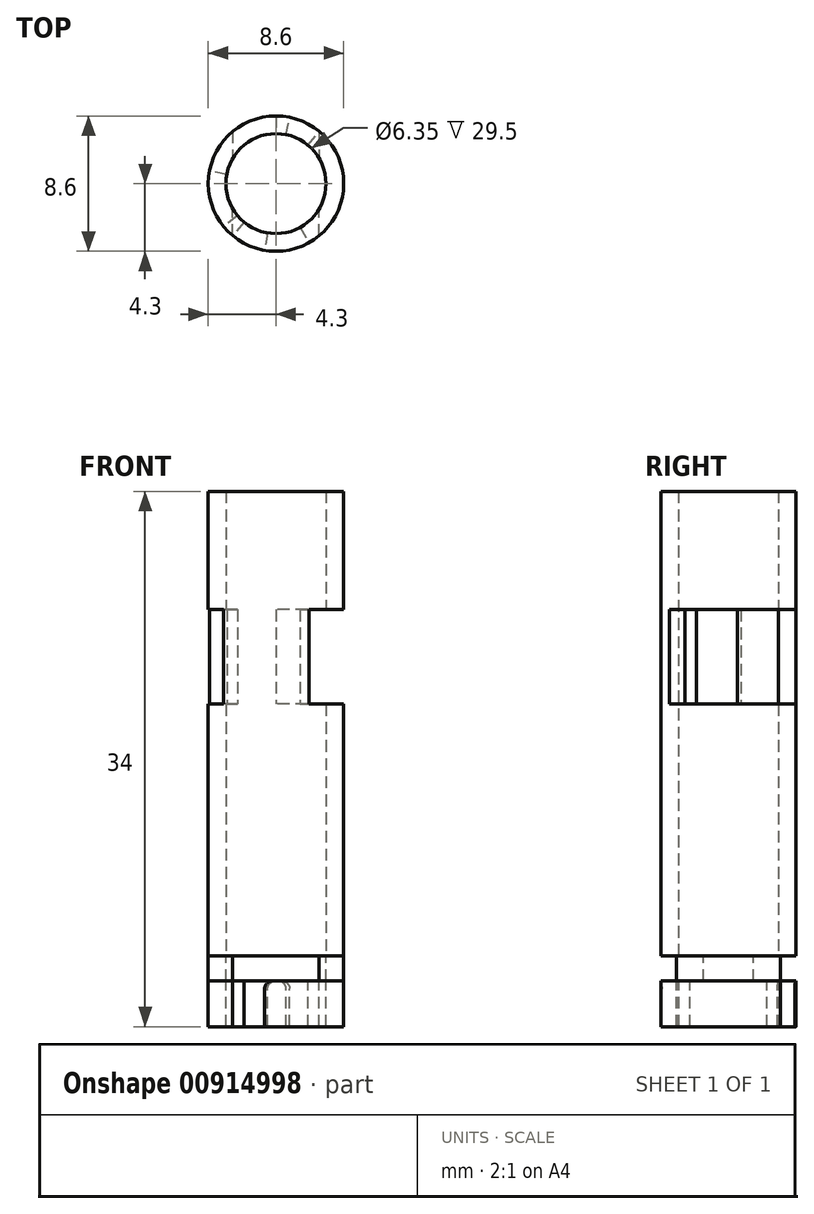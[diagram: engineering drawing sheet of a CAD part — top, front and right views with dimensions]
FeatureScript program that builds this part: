
annotation { "Feature Type Name" : "Feature", "Feature Type Description" : "" }
export const myFeature = defineFeature(function(context is Context, id is Id, definition is map)
    precondition{}
    {
        {
            var Q0;
            Q0=qCreatedBy(makeId("Top.planeOp"),FACE);
            var sketch = newSketch(context, id + "F0", { "sketchPlane" : qUnion([Q0])});
            skCircle(sketch, "E0", {"center": v(0, 0) * mm, "radius": 3.18 * mm});
            skCircle(sketch, "E1", {"center": v(0, 0) * mm, "radius": 4.3 * mm});
            skSolve(sketch);
        }
        {
            var Q0;
            Q0=makeQuery(id+"F0.imprint","IMPRINT",FACE,{"disambiguationData":[TD([[makeQuery(id+"F0.imprint","IMPRINT",EDGE,{"derivedFrom":sQuery(id+"F0.wireOp",EDGE,"E0")}),-1.0]])]});
            extrude(context, id + "F1", {"entities" : qUnion([Q0]), "depth" : 16 * mm, "offsetDistance" : 25.4 * mm});
        }
        {
            var Q0;
            Q0=makeQuery(id+"F1.opExtrude","CAP_FACE",FACE,{"disambiguationData":[OSD([sQuery(id+"F0.wireOp",EDGE,"E0"),sQuery(id+"F0.wireOp",EDGE,"E1")])],"isStart":false});
            var sketch = newSketch(context, id + "F2", { "sketchPlane" : qUnion([Q0])});
            skLineSegment(sketch, "E2", {"start": v(0, 4.3) * mm, "end": v(0, 3.17) * mm});
            skLineSegment(sketch, "E3", {"start": v(0, 0) * mm, "end": v(1.54, -2.78) * mm, "construction": true});
            skLineSegment(sketch, "E4", {"start": v(1.54, -2.78) * mm, "end": v(2.08, -3.76) * mm});
            skLineSegment(sketch, "E5", {"start": v(0, 0) * mm, "end": v(-2.45, -2.02) * mm});
            skLineSegment(sketch, "E6", {"start": v(0, 0) * mm, "end": v(-3.12, 0.58) * mm, "construction": true});
            skLineSegment(sketch, "E7", {"start": v(0, 3.17) * mm, "end": v(0, 0) * mm, "construction": true});
            skLineSegment(sketch, "E8", {"start": v(0, 0) * mm, "end": v(3.07, 0.8) * mm, "construction": true});
            skLineSegment(sketch, "E9", {"start": v(0, 0) * mm, "end": v(0.93, -3.04) * mm, "construction": true});
            skLineSegment(sketch, "E10", {"start": v(0.93, -3.04) * mm, "end": v(1.26, -4.11) * mm});
            skLineSegment(sketch, "E11", {"start": v(0, 0) * mm, "end": v(-1.54, 2.78) * mm, "construction": true});
            skLineSegment(sketch, "E12", {"start": v(0, 0) * mm, "end": v(-1.95, 2.5) * mm, "construction": true});
            skLineSegment(sketch, "E13", {"start": v(0, 0) * mm, "end": v(-1.09, 2.98) * mm, "construction": true});
            skLineSegment(sketch, "E14", {"start": v(-1.95, 2.5) * mm, "end": v(-2.65, 3.39) * mm});
            skLineSegment(sketch, "E15", {"start": v(-1.54, 2.78) * mm, "end": v(-2.08, 3.76) * mm});
            skLineSegment(sketch, "E16", {"start": v(-1.09, 2.98) * mm, "end": v(-1.47, 4.04) * mm});
            skLineSegment(sketch, "E17", {"start": v(0, 0) * mm, "end": v(-3.07, -0.8) * mm, "construction": true});
            skLineSegment(sketch, "E18", {"start": v(-3.12, 0.58) * mm, "end": v(-3.07, -0.8) * mm, "construction": true});
            skLineSegment(sketch, "E19", {"start": v(-3.07, -0.8) * mm, "end": v(-2.45, -2.02) * mm, "construction": true});
            skLineSegment(sketch, "E20", {"start": v(0, 3.17) * mm, "end": v(3.07, 0.8) * mm, "construction": true});
            skLineSegment(sketch, "E21", {"start": v(3.07, 0.8) * mm, "end": v(1.54, -2.78) * mm, "construction": true});
            skLineSegment(sketch, "E22", {"start": v(-3.12, 0.58) * mm, "end": v(-4.23, 0.78) * mm});
            skLineSegment(sketch, "E23", {"start": v(-2.45, -2.02) * mm, "end": v(-3.32, -2.74) * mm});
            skSolve(sketch);
        }
        {
            var Q0;
            {var subQ0=sQuery(id+"F2.wireOp",EDGE,"E2");Q0=makeQuery(id+"F2.imprint","IMPRINT",FACE,{"disambiguationData":[TD([[makeQuery(id+"F2.imprint","IMPRINT",EDGE,{"derivedFrom":subQ0}),-1.0]])]});}
            var Q1;
            {var subQ0=sQuery(id+"F2.wireOp",EDGE,"eu6biRq1-f5Uw-FhgU-ruvT-oJqhQKLmv7p4");Q1=makeQuery(id+"F2.imprint","IMPRINT",FACE,{"disambiguationData":[TD([[makeQuery(id+"F2.imprint","IMPRINT",EDGE,{"derivedFrom":subQ0}),1.0]])]});}
            var Q2;
            {var subQ0=sQuery(id+"F2.wireOp",EDGE,"E4");Q2=makeQuery(id+"F2.imprint","IMPRINT",FACE,{"disambiguationData":[TD([[makeQuery(id+"F2.imprint","IMPRINT",EDGE,{"derivedFrom":subQ0}),-1.0]])]});}
            var Q3;
            {var subQ0=sQuery(id+"F2.wireOp",EDGE,"WfiJlDDU-s9re-JO37-0JUV-52wj0VNvj8No");Q3=makeQuery(id+"F2.imprint","IMPRINT",FACE,{"disambiguationData":[TD([[makeQuery(id+"F2.imprint","IMPRINT",EDGE,{"derivedFrom":subQ0}),-1.0]])]});}
            var Q4;
            {var subQ0=sQuery(id+"F2.wireOp",EDGE,"E14");Q4=makeQuery(id+"F2.imprint","IMPRINT",FACE,{"disambiguationData":[TD([[makeQuery(id+"F2.imprint","IMPRINT",EDGE,{"derivedFrom":subQ0}),-1.0]])]});}
            var Q5;
            {var subQ0=sQuery(id+"F2.wireOp",EDGE,"E15");Q5=makeQuery(id+"F2.imprint","IMPRINT",FACE,{"disambiguationData":[TD([[makeQuery(id+"F2.imprint","IMPRINT",EDGE,{"derivedFrom":subQ0}),-1.0]])]});}
            var Q6;
            {var subQ0=sQuery(id+"F2.wireOp",EDGE,"E10");Q6=makeQuery(id+"F2.imprint","IMPRINT",FACE,{"disambiguationData":[TD([[makeQuery(id+"F2.imprint","IMPRINT",EDGE,{"derivedFrom":subQ0}),-1.0]])]});}
            var Q7;
            {var subQ0=sQuery(id+"F2.wireOp",EDGE,"E14");Q7=makeQuery(id+"F2.imprint","IMPRINT",FACE,{"disambiguationData":[TD([[makeQuery(id+"F2.imprint","IMPRINT",EDGE,{"derivedFrom":subQ0}),1.0]])]});}
            extrude(context, id + "F3", {"entities" : qUnion([Q0, Q1, Q2, Q3, Q4, Q5, Q6, Q7]), "operationType" : NewBodyOperationType.ADD, "depth" : 6 * mm, "offsetDistance" : 25.4 * mm});
        }
        {
            var Q0;
            Q0=makeQuery(id+"F3.opExtrude","CAP_FACE",FACE,{"disambiguationData":[OSD([sQuery(id+"F0.wireOp",EDGE,"E0"),sQuery(id+"F0.wireOp",EDGE,"E1"),sQuery(id+"F2.wireOp",EDGE,"E2"),sQuery(id+"F2.wireOp",EDGE,"E16")])],"isStart":false});
            var sketch = newSketch(context, id + "F4", { "sketchPlane" : qUnion([Q0])});
            skCircle(sketch, "E24", {"center": v(0, 0) * mm, "radius": 3.18 * mm});
            skCircle(sketch, "E25", {"center": v(0, 0) * mm, "radius": 4.3 * mm});
            skSolve(sketch);
        }
        {
            var Q0;
            Q0=makeQuery(id+"F4.imprint","IMPRINT",FACE,{"disambiguationData":[TD([[makeQuery(id+"F4.imprint","IMPRINT",EDGE,{"derivedFrom":sQuery(id+"F4.wireOp",EDGE,"E25")}),1.0]])]});
            extrude(context, id + "F5", {"entities" : qUnion([Q0]), "operationType" : NewBodyOperationType.ADD, "depth" : 7.5 * mm, "offsetDistance" : 25.4 * mm});
        }
        {
            var Q0;
            Q0=qCreatedBy(makeId("Top.planeOp"),FACE);
            var sketch = newSketch(context, id + "F6", { "sketchPlane" : qUnion([Q0])});
            skCircle(sketch, "E26", {"center": v(0, 0) * mm, "radius": 3.18 * mm});
            skCircle(sketch, "E27", {"center": v(0, 0) * mm, "radius": 4.3 * mm});
            skLineSegment(sketch, "E28", {"start": v(-2.75, -3.3) * mm, "end": v(-2.75, -1.59) * mm});
            skLineSegment(sketch, "E29", {"start": v(2.75, -3.3) * mm, "end": v(2.75, -1.59) * mm});
            skLineSegment(sketch, "E30", {"start": v(-2.75, -1.59) * mm, "end": v(0, 0) * mm, "construction": true});
            skLineSegment(sketch, "E31", {"start": v(2.75, -1.59) * mm, "end": v(0, 0) * mm, "construction": true});
            skLineSegment(sketch, "E32.MirrorCS", {"start": v(2.75, 1.59) * mm, "end": v(0, 0) * mm, "construction": true});
            skLineSegment(sketch, "E33.MirrorCS", {"start": v(-2.75, 1.59) * mm, "end": v(0, 0) * mm, "construction": true});
            skLineSegment(sketch, "E34.MirrorCS", {"start": v(-2.75, 3.3) * mm, "end": v(-2.75, 1.59) * mm});
            skLineSegment(sketch, "E35.MirrorCS", {"start": v(2.75, 3.3) * mm, "end": v(2.75, 1.59) * mm});
            skSolve(sketch);
        }
        {
            var Q0;
            {var subQ0=sQuery(id+"F6.wireOp",EDGE,"E28");Q0=makeQuery(id+"F6.imprint","IMPRINT",FACE,{"disambiguationData":[TD([[makeQuery(id+"F6.imprint","IMPRINT",EDGE,{"derivedFrom":subQ0}),1.0]])]});}
            var Q1;
            {var subQ0=sQuery(id+"F6.wireOp",EDGE,"E29");Q1=makeQuery(id+"F6.imprint","IMPRINT",FACE,{"disambiguationData":[TD([[makeQuery(id+"F6.imprint","IMPRINT",EDGE,{"derivedFrom":subQ0}),-1.0]])]});}
            extrude(context, id + "F7", {"entities" : qUnion([Q0, Q1]), "oppositeDirection" : true, "depth" : 1.6 * mm, "offsetDistance" : 25.4 * mm});
        }
        {
            var Q0;
            Q0=makeQuery(id+"F7.opExtrude","CAP_FACE",FACE,{"disambiguationData":[OSD([sQuery(id+"F6.wireOp",EDGE,"E26"),sQuery(id+"F6.wireOp",EDGE,"E27"),sQuery(id+"F6.wireOp",EDGE,"E28"),sQuery(id+"F6.wireOp",EDGE,"E29")])],"isStart":false});
            var sketch = newSketch(context, id + "F8", { "sketchPlane" : qUnion([Q0])});
            skCircle(sketch, "E36", {"center": v(0, 0) * mm, "radius": 4.3 * mm});
            skCircle(sketch, "E37", {"center": v(0, 0) * mm, "radius": 3.18 * mm});
            skLineSegment(sketch, "E38", {"start": v(0, 0) * mm, "end": v(-2.03, 2.44) * mm, "construction": true});
            skLineSegment(sketch, "E39", {"start": v(0, 0) * mm, "end": v(-0.54, 3.13) * mm, "construction": true});
            skLineSegment(sketch, "E40", {"start": v(0, 0) * mm, "end": v(0.65, -3.1) * mm, "construction": true});
            skLineSegment(sketch, "E41", {"start": v(0, 0) * mm, "end": v(2.03, -2.44) * mm, "construction": true});
            skLineSegment(sketch, "E42", {"start": v(-2.75, 1.59) * mm, "end": v(-2.75, 3.3) * mm});
            skLineSegment(sketch, "E43", {"start": v(-2.03, 2.44) * mm, "end": v(-2.75, 1.59) * mm});
            skLineSegment(sketch, "E44", {"start": v(-2.03, 2.44) * mm, "end": v(-2.75, 3.3) * mm});
            skLineSegment(sketch, "E45", {"start": v(2.03, -2.44) * mm, "end": v(2.75, -3.3) * mm});
            skLineSegment(sketch, "E46", {"start": v(-0.54, 3.13) * mm, "end": v(-0.73, 4.24) * mm});
            skLineSegment(sketch, "E47", {"start": v(0.65, -3.1) * mm, "end": v(0.88, -4.2) * mm});
            skSolve(sketch);
        }
        {
            var Q0;
            {var subQ2=sQuery(id+"F8.wireOp",EDGE,"mCtkyoXV-Rd7h-jJL0-9tHd-2e0R4zRDDLDJ");Q0=makeQuery(id+"F8.imprint","IMPRINT",FACE,{"disambiguationData":[TD([[makeQuery(id+"F8.imprint","IMPRINT",EDGE,{"derivedFrom":subQ2}),-1.0]])]});}
            var Q1;
            {var subQ1=makeQuery(id+"F7.opExtrude","CAP_EDGE",EDGE,{"disambiguationData":[OSD([sQuery(id+"F6.wireOp",EDGE,"E29")])],"isStart":false});Q1=makeQuery(id+"F8.imprint","IMPRINT",FACE,{"disambiguationData":[TD([[makeQuery(id+"F8.imprint","IMPRINT",EDGE,{"derivedFrom":subQ1}),1.0]])]});}
            var Q2;
            {var subQ1=makeQuery(id+"F7.opExtrude","CAP_EDGE",EDGE,{"disambiguationData":[OSD([sQuery(id+"F6.wireOp",EDGE,"E28")])],"isStart":false});Q2=makeQuery(id+"F8.imprint","IMPRINT",FACE,{"disambiguationData":[TD([[makeQuery(id+"F8.imprint","IMPRINT",EDGE,{"derivedFrom":subQ1}),-1.0]])]});}
            var Q3;
            {var subQ2=sQuery(id+"F8.wireOp",EDGE,"NMcYGIYV-T0NB-F5BN-H1pw-wRnPyMwqkAcY");Q3=makeQuery(id+"F8.imprint","IMPRINT",FACE,{"disambiguationData":[TD([[makeQuery(id+"F8.imprint","IMPRINT",EDGE,{"derivedFrom":subQ2}),-1.0]])]});}
            var Q4;
            {var subQ0=sQuery(id+"F8.wireOp",EDGE,"E42");Q4=makeQuery(id+"F8.imprint","IMPRINT",FACE,{"disambiguationData":[TD([[makeQuery(id+"F8.imprint","IMPRINT",EDGE,{"derivedFrom":subQ0}),-1.0]])]});}
            var Q5;
            {var subQ1=sQuery(id+"F8.wireOp",EDGE,"E42");Q5=makeQuery(id+"F8.imprint","IMPRINT",FACE,{"disambiguationData":[TD([[makeQuery(id+"F8.imprint","IMPRINT",EDGE,{"derivedFrom":subQ1}),1.0]])]});}
            var Q6;
            {var subQ2=sQuery(id+"F8.wireOp",EDGE,"E46");Q6=makeQuery(id+"F8.imprint","IMPRINT",FACE,{"disambiguationData":[TD([[makeQuery(id+"F8.imprint","IMPRINT",EDGE,{"derivedFrom":subQ2}),-1.0]])]});}
            var Q7;
            {var subQ2=sQuery(id+"F8.wireOp",EDGE,"E47");Q7=makeQuery(id+"F8.imprint","IMPRINT",FACE,{"disambiguationData":[TD([[makeQuery(id+"F8.imprint","IMPRINT",EDGE,{"derivedFrom":subQ2}),-1.0]])]});}
            var Q8;
            {var subQ2=sQuery(id+"F8.wireOp",EDGE,"E45");Q8=makeQuery(id+"F8.imprint","IMPRINT",FACE,{"disambiguationData":[TD([[makeQuery(id+"F8.imprint","IMPRINT",EDGE,{"derivedFrom":subQ2}),1.0]])]});}
            extrude(context, id + "F9", {"entities" : qUnion([Q0, Q1, Q2, Q3, Q4, Q5, Q6, Q7, Q8]), "depth" : 2.9 * mm, "offsetDistance" : 25.4 * mm});
        }
        {
            var Q0;
            Q0=makeQuery(id+"F9.opExtrude","CAP_EDGE",EDGE,{"disambiguationData":[OSD([sQuery(id+"F8.wireOp",EDGE,"E47")])],"isStart":true});
            var Q1;
            Q1=makeQuery(id+"F9.opExtrude","CAP_EDGE",EDGE,{"disambiguationData":[OSD([sQuery(id+"F8.wireOp",EDGE,"E46")])],"isStart":true});
            fillet(context, id + "F10", {"entities" : qUnion([Q0, Q1]), "radius" : .5 * mm, "tangentPropagation" : true, "allowEdgeOverflow" : false});
        }
    });
